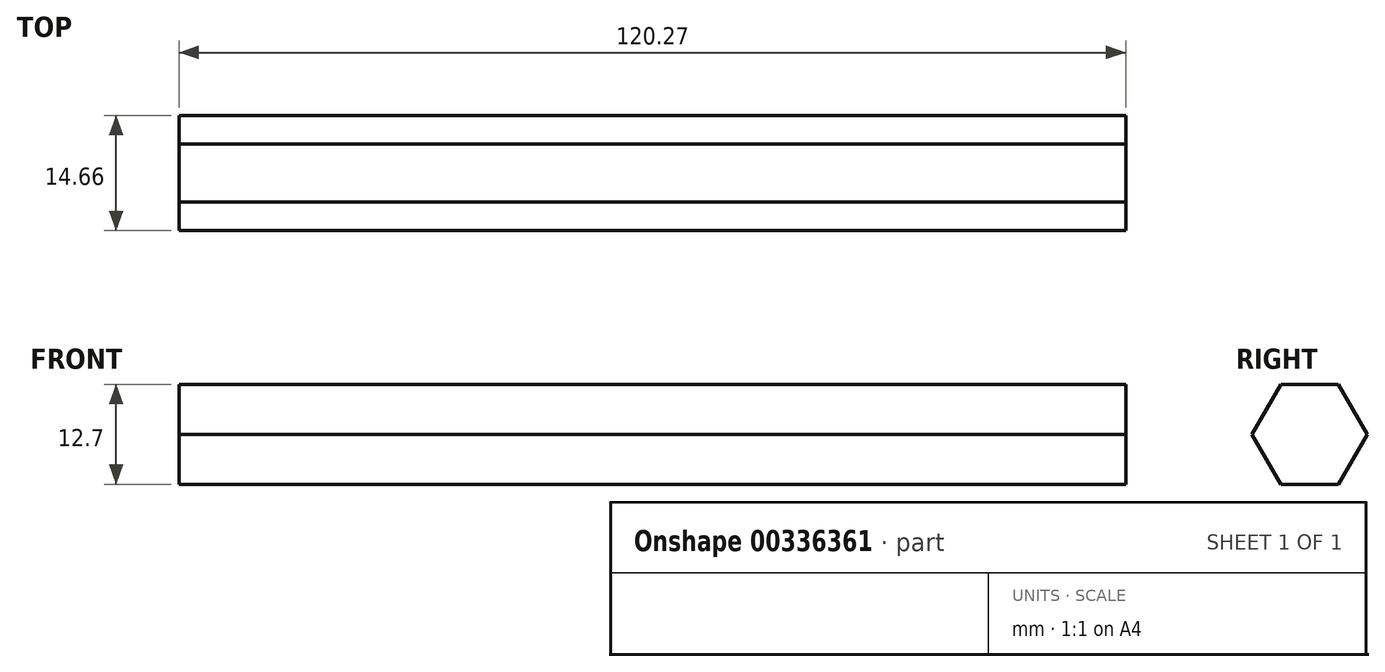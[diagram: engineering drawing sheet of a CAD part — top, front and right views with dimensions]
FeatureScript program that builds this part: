
annotation { "Feature Type Name" : "Feature", "Feature Type Description" : "" }
export const myFeature = defineFeature(function(context is Context, id is Id, definition is map)
    precondition{}
    {
        {
            var Q0;
            Q0=qCreatedBy(makeId("Right.planeOp"),FACE);
            var sketch = newSketch(context, id + "F0", { "sketchPlane" : qUnion([Q0])});
            skCircle(sketch, "E0.cCircle", {"center": v(0, 0) * mm, "radius": 6.35 * mm, "construction": true});
            skLineSegment(sketch, "E0.0", {"start": v(-3.67, 6.35) * mm, "end": v(3.67, 6.35) * mm});
            skLineSegment(sketch, "E0.1", {"start": v(3.67, 6.35) * mm, "end": v(7.33, 0) * mm});
            skLineSegment(sketch, "E0.2", {"start": v(7.33, 0) * mm, "end": v(3.67, -6.35) * mm});
            skLineSegment(sketch, "E0.3", {"start": v(3.67, -6.35) * mm, "end": v(-3.67, -6.35) * mm});
            skLineSegment(sketch, "E0.4", {"start": v(-3.67, -6.35) * mm, "end": v(-7.33, 0) * mm});
            skLineSegment(sketch, "E0.5", {"start": v(-7.33, 0) * mm, "end": v(-3.67, 6.35) * mm});
            skPoint(sketch, "E0.0.midPoint", {"position": v(0, 6.35) * mm});
            skSolve(sketch);
        }
        {
            var Q0;
            Q0=makeQuery(id+"F0.imprint","IMPRINT",FACE,{"disambiguationData":[TD([[makeQuery(id+"F0.imprint","IMPRINT",EDGE,{"derivedFrom":sQuery(id+"F0.wireOp",EDGE,"E0.0")}),-1.0]])]});
            extrude(context, id + "F1", {"entities" : qUnion([Q0]), "depth" : 120.27 * mm});
        }
    });
